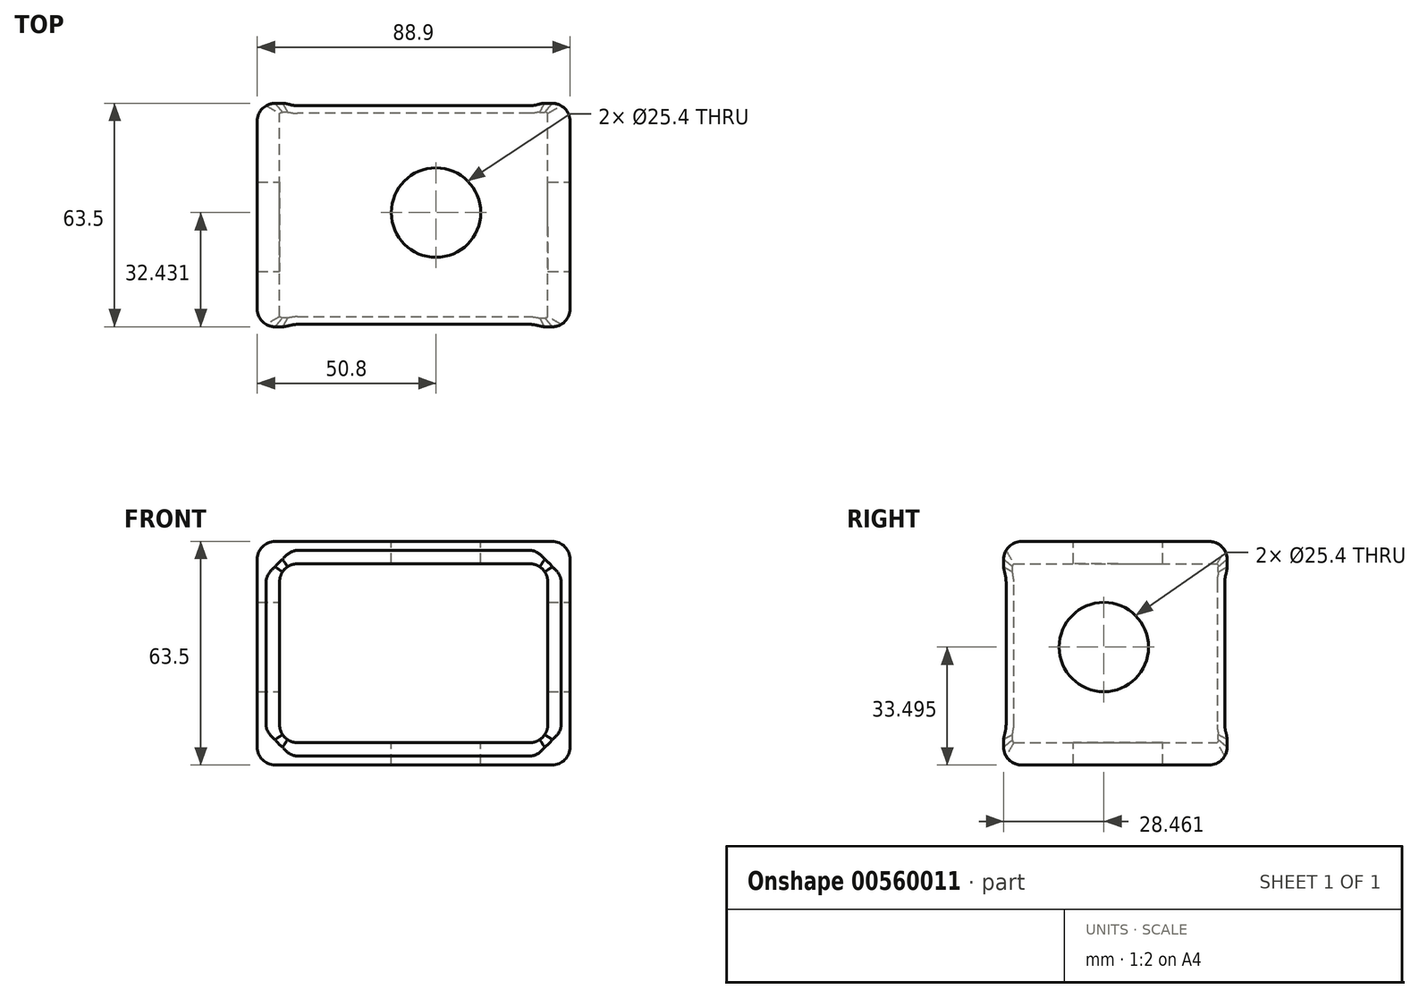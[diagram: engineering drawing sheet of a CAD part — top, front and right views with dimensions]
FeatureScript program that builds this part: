
annotation { "Feature Type Name" : "Feature", "Feature Type Description" : "" }
export const myFeature = defineFeature(function(context is Context, id is Id, definition is map)
    precondition{}
    {
        {
            var Q0;
            Q0=qCreatedBy(makeId("Front.planeOp"),FACE);
            var sketch = newSketch(context, id + "F0", { "sketchPlane" : qUnion([Q0])});
            skLineSegment(sketch, "E0.bottom", {"start": v(0, 0) * mm, "end": v(-88.9, 0) * mm});
            skLineSegment(sketch, "E0.top", {"start": v(0, 63.5) * mm, "end": v(-88.9, 63.5) * mm});
            skLineSegment(sketch, "E0.left", {"start": v(0, 0) * mm, "end": v(0, 63.5) * mm});
            skLineSegment(sketch, "E0.right", {"start": v(-88.9, 0) * mm, "end": v(-88.9, 63.5) * mm});
            skLineSegment(sketch, "E1.bottom", {"start": v(-6.35, 6.35) * mm, "end": v(-82.55, 6.35) * mm});
            skLineSegment(sketch, "E1.top", {"start": v(-6.35, 57.15) * mm, "end": v(-82.55, 57.15) * mm});
            skLineSegment(sketch, "E1.left", {"start": v(-6.35, 6.35) * mm, "end": v(-6.35, 57.15) * mm});
            skLineSegment(sketch, "E1.right", {"start": v(-82.55, 6.35) * mm, "end": v(-82.55, 57.15) * mm});
            skSolve(sketch);
        }
        {
            var Q0;
            Q0 = qSketchRegion(id + "F0", true);
            extrude(context, id + "F1", {"entities" : qUnion([Q0]), "depth" : 63.5 * mm, "offsetDistance" : 25.4 * mm});
        }
        {
            var Q0;
            Q0=makeQuery(id+"F1.opExtrude","SWEPT_FACE",FACE,{"disambiguationData":[OSD([sQuery(id+"F0.wireOp",EDGE,"E0.top")])]});
            var Q1;
            Q1=makeQuery(id+"F1.opExtrude","SWEPT_FACE",FACE,{"disambiguationData":[OSD([sQuery(id+"F0.wireOp",EDGE,"E0.bottom")])]});
            var Q2;
            Q2=makeQuery(id+"F1.opExtrude","SWEPT_FACE",FACE,{"disambiguationData":[OSD([sQuery(id+"F0.wireOp",EDGE,"E0.right")])]});
            var Q3;
            Q3=makeQuery(id+"F1.opExtrude","SWEPT_FACE",FACE,{"disambiguationData":[OSD([sQuery(id+"F0.wireOp",EDGE,"E0.left")])]});
            var Q4;
            Q4=makeQuery(id+"F1.opExtrude","SWEPT_EDGE",EDGE,{"disambiguationData":[OSD([sQuery(id+"F0.wireOp",EDGE,"E1.bottom"),sQuery(id+"F0.wireOp",EDGE,"E1.right")])]});
            var Q5;
            Q5=makeQuery(id+"F1.opExtrude","SWEPT_EDGE",EDGE,{"disambiguationData":[OSD([sQuery(id+"F0.wireOp",EDGE,"E1.top"),sQuery(id+"F0.wireOp",EDGE,"E1.right")])]});
            var Q6;
            Q6=makeQuery(id+"F1.opExtrude","SWEPT_EDGE",EDGE,{"disambiguationData":[OSD([sQuery(id+"F0.wireOp",EDGE,"E1.top"),sQuery(id+"F0.wireOp",EDGE,"E1.left")])]});
            var Q7;
            Q7=makeQuery(id+"F1.opExtrude","SWEPT_EDGE",EDGE,{"disambiguationData":[OSD([sQuery(id+"F0.wireOp",EDGE,"E1.bottom"),sQuery(id+"F0.wireOp",EDGE,"E1.left")])]});
            fillet(context, id + "F2", {"entities" : qUnion([Q0, Q1, Q2, Q3, Q4, Q5, Q6, Q7]), "radius" : 5.08 * mm, "tangentPropagation" : true, "allowEdgeOverflow" : false});
        }
        {
            var Q0;
            Q0=makeQuery(id+"F1.opExtrude","CAP_EDGE",EDGE,{"disambiguationData":[OSD([sQuery(id+"F0.wireOp",EDGE,"E1.top")])],"isStart":false});
            var Q1;
            Q1=makeQuery(id+"F1.opExtrude","CAP_EDGE",EDGE,{"disambiguationData":[OSD([sQuery(id+"F0.wireOp",EDGE,"E1.top")])],"isStart":true});
            chamfer(context, id + "F3", {"entities" : qUnion([Q0, Q1]), "width" : 2.54 * mm, "tangentPropagation" : true});
        }
        {
            var Q0;
            Q0=makeQuery(id+"F1.opExtrude","SWEPT_FACE",FACE,{"disambiguationData":[OSD([sQuery(id+"F0.wireOp",EDGE,"E0.top")])]});
            var sketch = newSketch(context, id + "F4", { "sketchPlane" : qUnion([Q0])});
            skCircle(sketch, "E2", {"center": v(-38.1, -31.07) * mm, "radius": 12.7 * mm});
            skSolve(sketch);
        }
        {
            var Q0;
            Q0 = qSketchRegion(id + "F4", true);
            var Q1;
            Q1=makeQuery(id+"F1.opExtrude","SWEPT_FACE",FACE,{"disambiguationData":[OSD([sQuery(id+"F0.wireOp",EDGE,"E0.bottom")])]});
            extrude(context, id + "F5", {"entities" : qUnion([Q0]), "operationType" : NewBodyOperationType.REMOVE, "endBound" : BoundingType.UP_TO_SURFACE, "oppositeDirection" : true, "depth" : 25.4 * mm, "endBoundEntityFace" : qUnion([Q1]), "offsetDistance" : 25.4 * mm});
        }
        {
            var Q0;
            Q0=makeQuery(id+"F1.opExtrude","SWEPT_FACE",FACE,{"disambiguationData":[OSD([sQuery(id+"F0.wireOp",EDGE,"E0.left")])]});
            var sketch = newSketch(context, id + "F6", { "sketchPlane" : qUnion([Q0])});
            skCircle(sketch, "E3", {"center": v(-35.04, 33.5) * mm, "radius": 12.7 * mm});
            skSolve(sketch);
        }
        {
            var Q0;
            Q0 = qSketchRegion(id + "F6", true);
            var Q1;
            Q1=makeQuery(id+"F1.opExtrude","SWEPT_FACE",FACE,{"disambiguationData":[OSD([sQuery(id+"F0.wireOp",EDGE,"E0.right")])]});
            extrude(context, id + "F7", {"entities" : qUnion([Q0]), "operationType" : NewBodyOperationType.REMOVE, "endBound" : BoundingType.UP_TO_SURFACE, "oppositeDirection" : true, "depth" : 25.4 * mm, "endBoundEntityFace" : qUnion([Q1]), "offsetDistance" : 25.4 * mm});
        }
    });
